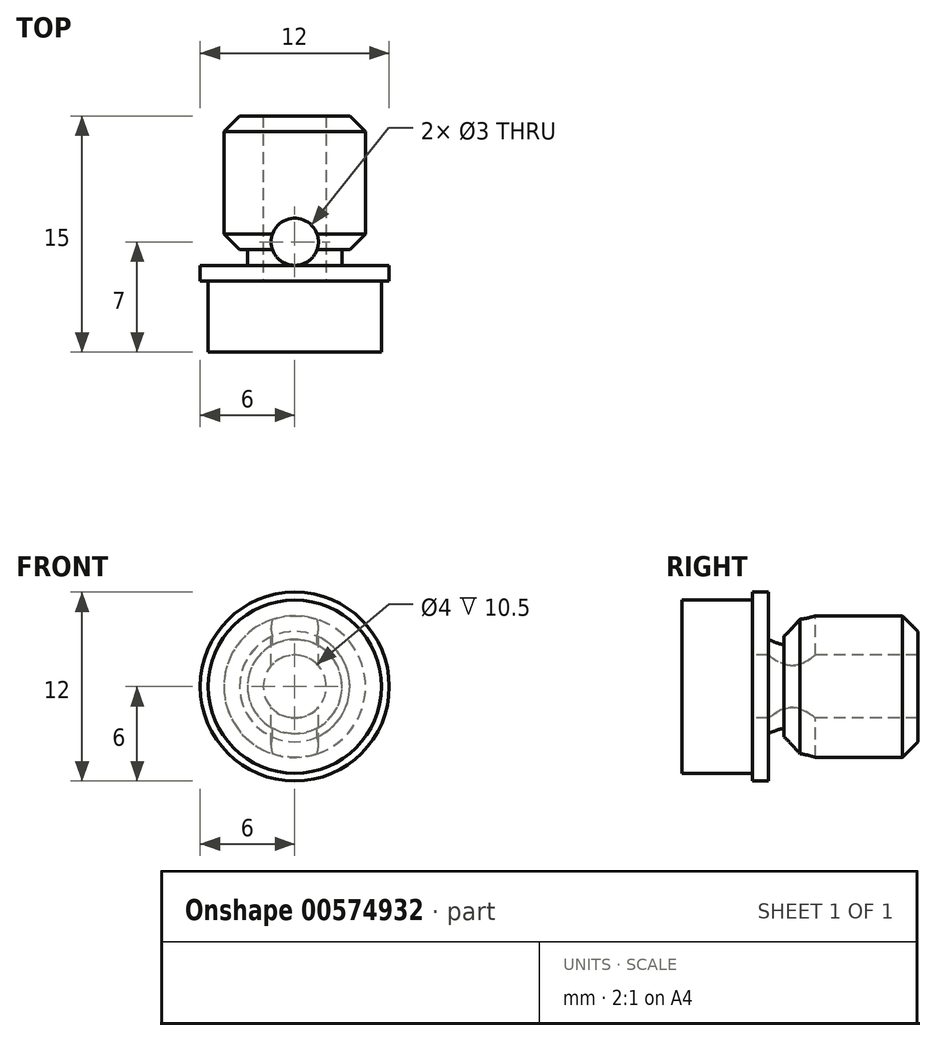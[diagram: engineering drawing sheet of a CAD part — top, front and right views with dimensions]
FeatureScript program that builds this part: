
annotation { "Feature Type Name" : "Feature", "Feature Type Description" : "" }
export const myFeature = defineFeature(function(context is Context, id is Id, definition is map)
    precondition{}
    {
        {
            var Q0;
            Q0=qCreatedBy(makeId("Right.planeOp"),FACE);
            var sketch = newSketch(context, id + "F0", { "sketchPlane" : qUnion([Q0])});
            skLineSegment(sketch, "E0", {"start": v(0, 5.5) * mm, "end": v(4.5, 5.5) * mm});
            skLineSegment(sketch, "E1", {"start": v(4.5, 5.5) * mm, "end": v(4.5, 6) * mm});
            skLineSegment(sketch, "E2", {"start": v(4.5, 6) * mm, "end": v(5.5, 6) * mm});
            skLineSegment(sketch, "E3", {"start": v(5.5, 6) * mm, "end": v(5.5, 3) * mm});
            skLineSegment(sketch, "E4", {"start": v(15, 4.5) * mm, "end": v(15, 2) * mm});
            skLineSegment(sketch, "E5", {"start": v(15, 2) * mm, "end": v(4.5, 2) * mm});
            skLineSegment(sketch, "E6", {"start": v(4.5, 2) * mm, "end": v(4.5, 0) * mm});
            skLineSegment(sketch, "E7", {"start": v(0, 5.5) * mm, "end": v(0, 0) * mm});
            skLineSegment(sketch, "E8", {"start": v(0, 0) * mm, "end": v(17.48, 0) * mm, "construction": true});
            skLineSegment(sketch, "E9", {"start": v(0, 0) * mm, "end": v(4.5, 0) * mm});
            skLineSegment(sketch, "E10", {"start": v(15, 4.5) * mm, "end": v(6.5, 4.5) * mm});
            skLineSegment(sketch, "E11", {"start": v(5.5, 3) * mm, "end": v(6.5, 3) * mm});
            skLineSegment(sketch, "E12", {"start": v(6.5, 3) * mm, "end": v(6.5, 4.5) * mm});
            skSolve(sketch);
        }
        {
            var Q0;
            Q0 = qSketchRegion(id + "F0", true);
            var Q1;
            Q1=sQuery(id+"F0.wireOp",EDGE,"E8");
            revolve(context, id + "F1", {"entities" : qUnion([Q0]), "axis" : qUnion([Q1]), "revolveType" : RevolveType.FULL});
        }
        {
            var Q0;
            Q0=makeQuery(id+"F1.opRevolve","SWEPT_EDGE",EDGE,{"disambiguationData":[OSD([sQuery(id+"F0.wireOp",EDGE,"E4"),sQuery(id+"F0.wireOp",EDGE,"E10")])]});
            var Q1;
            Q1=makeQuery(id+"F1.opRevolve","SWEPT_EDGE",EDGE,{"disambiguationData":[OSD([sQuery(id+"F0.wireOp",EDGE,"E10"),sQuery(id+"F0.wireOp",EDGE,"E12")])]});
            chamfer(context, id + "F2", {"entities" : qUnion([Q0, Q1]), "width" : 1 * mm, "tangentPropagation" : true});
        }
        {
            var Q0;
            Q0=qCreatedBy(makeId("Top.planeOp"),FACE);
            var sketch = newSketch(context, id + "F3", { "sketchPlane" : qUnion([Q0])});
            skCircle(sketch, "E13", {"center": v(0, 7) * mm, "radius": 1.5 * mm});
            skSolve(sketch);
        }
        {
            var Q0;
            Q0 = qSketchRegion(id + "F3", true);
            extrude(context, id + "F4", {"entities" : qUnion([Q0]), "operationType" : NewBodyOperationType.REMOVE, "oppositeDirection" : true, "depth" : 50 * mm, "offsetDistance" : 25 * mm, "symmetric" : true});
        }
    });
